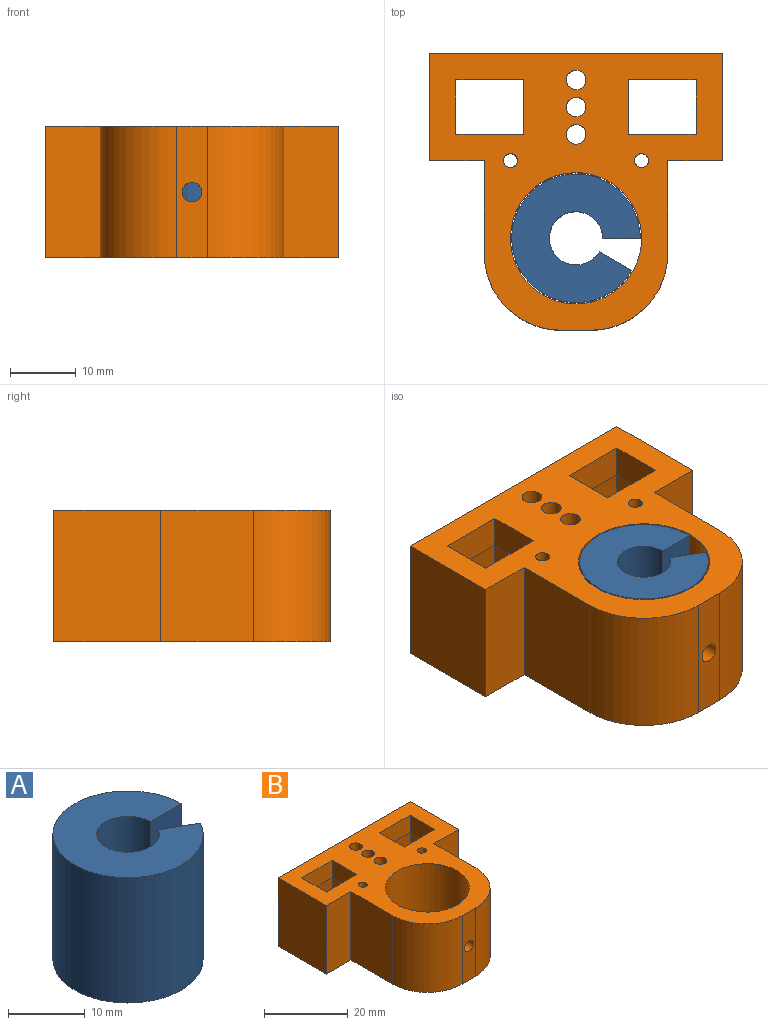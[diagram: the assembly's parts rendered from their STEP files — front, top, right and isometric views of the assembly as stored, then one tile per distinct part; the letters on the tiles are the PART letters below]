
ASSEMBLY  parts=2 mates=1
PART A: 6 faces, bbox 19.6x19.6x20 mm
  f0: cylinder r=4.07mm len=20mm, axis (0,0,-1), area 468.8mm2, adj f1,f3,f4,f5
  f1: plane 20x5.73mm, normal (0,-1,0), area 114.6mm2, adj f0,f2,f4,f5
  f2: cylinder r=9.8mm len=20mm, axis (0,0,-1), area 1128.9mm2, adj f1,f3,f4,f5
  f3: plane 20x4.96mm, normal (0.5,0.87,0), area 114.6mm2, adj f0,f2,f4,f5
  f4: plane 19.6x19.6mm, normal (0,0,1), area 228.9mm2, adj f0,f1,f2,f3
  f5: plane 19.6x19.6mm, normal (0,0,-1), area 228.9mm2, adj f0,f1,f2,f3
PART B: 35 faces, bbox 44.6x42.2x20 mm
  f0: cylinder r=10mm len=20mm, axis (0,0,-1), area 1249.6mm2, adj f24,f25,f26
  f1: plane 10.3x5mm, normal (0,-1,0), area 51.5mm2, adj f2,f23,f24,f30
  f2: plane 8.3x5mm, normal (-1,0,0), area 41.5mm2, adj f1,f3,f24,f28
  f3: plane 10.3x5mm, normal (0,1,0), area 51.5mm2, adj f2,f23,f24,f27
  f4: plane 44.6x20mm, normal (0,1,0), area 892mm2, adj f5,f16,f24,f25
  f5: plane 20x16.3mm, normal (-1,0,0), area 326mm2, adj f4,f6,f24,f25
  f6: plane 20x8.3mm, normal (0,-1,0), area 166mm2, adj f5,f7,f24,f25
  f7: plane 20x14.15mm, normal (-1,0,0), area 283mm2, adj f6,f8,f24,f25
  f8: cylinder r=11.7mm len=20mm, axis (0,0,-1), area 367.6mm2, adj f7,f9,f24,f25
  f9: plane 20x4.6mm, normal (0,-1,0), area 84.9mm2, adj f8,f10,f24,f25,f26
  f10: cylinder r=11.7mm len=20mm, axis (0,0,-1), area 367.6mm2, adj f9,f11,f24,f25
  f11: plane 20x14.15mm, normal (1,0,0), area 283mm2, adj f10,f12,f24,f25
  f12: plane 20x8.3mm, normal (0,-1,0), area 166mm2, adj f11,f16,f24,f25
  f13: plane 8.3x5mm, normal (1,0,0), area 41.5mm2, adj f14,f22,f24,f32
  f14: plane 10.3x5mm, normal (0,-1,0), area 51.5mm2, adj f13,f15,f24,f34
  f15: plane 8.3x5mm, normal (-1,0,0), area 41.5mm2, adj f14,f22,f24,f33
  f16: plane 20x16.3mm, normal (1,0,0), area 326mm2, adj f4,f12,f24,f25
  f17: cylinder r=1.5mm len=20mm, axis (0,0,-1), area 188.5mm2, adj f24,f25
  f18: cylinder r=1.06mm len=20mm, axis (0,0,-1), area 133.2mm2, adj f24,f25
  f19: cylinder r=1.5mm len=20mm, axis (0,0,-1), area 188.5mm2, adj f24,f25
  f20: cylinder r=1.5mm len=20mm, axis (0,0,-1), area 188.5mm2, adj f24,f25
  f21: cylinder r=1.06mm len=20mm, axis (0,0,-1), area 133.2mm2, adj f24,f25
  f22: plane 10.3x5mm, normal (0,1,0), area 51.5mm2, adj f13,f15,f24,f31
  f23: plane 8.3x5mm, normal (1,0,0), area 41.5mm2, adj f1,f3,f24,f29
  f24: plane 44.6x42.15mm, normal (0,0,1), area 878.6mm2, adj f0,f1,f2,f3,f4,f5,f6,f7
  f25: plane 44.6x42.15mm, normal (0,0,-1), area 796.2mm2, adj f0,f4,f5,f6,f7,f8,f9,f10
  f26: cylinder r=1.5mm len=4.11mm, axis (0,-1,0), area 38.2mm2, adj f0,f9
  f27: plane 15x12.3mm, normal (0,1,-0.07), area 169.9mm2, adj f3,f25,f28,f29
  f28: plane 15x10.3mm, normal (-1,0,-0.07), area 139.8mm2, adj f2,f25,f27,f30
  f29: plane 15x10.3mm, normal (1,0,-0.07), area 139.8mm2, adj f23,f25,f27,f30
  f30: plane 15x12.3mm, normal (0,-1,-0.07), area 169.9mm2, adj f1,f25,f28,f29
  f31: plane 15x12.3mm, normal (0,1,-0.07), area 169.9mm2, adj f22,f25,f32,f33
  f32: plane 15x10.3mm, normal (1,0,-0.07), area 139.8mm2, adj f13,f25,f31,f34
  f33: plane 15x10.3mm, normal (-1,0,-0.07), area 139.8mm2, adj f15,f25,f31,f34
  f34: plane 15x12.3mm, normal (0,-1,-0.07), area 169.9mm2, adj f14,f25,f32,f33
PLACE A t=(0.53,-19.52,-16.03)mm
PLACE B t=(-3.91,0.48,-16.03)mm
MATE fastened A.f0 <-> B.f0  axis (0,0,-1) through (-3.91,-19.52,-16.03)mm
